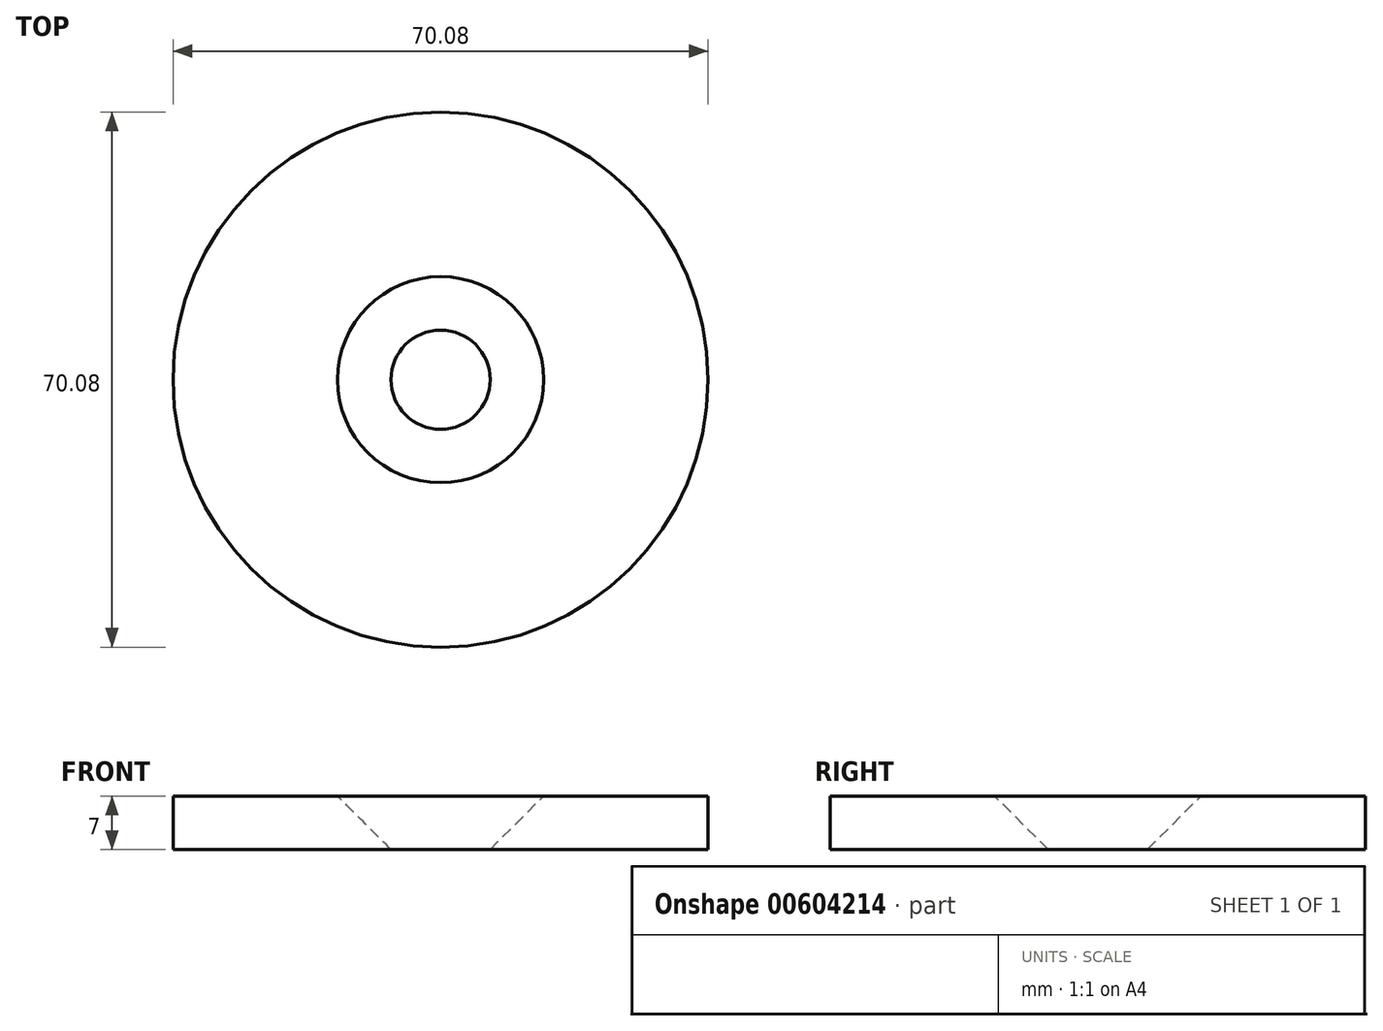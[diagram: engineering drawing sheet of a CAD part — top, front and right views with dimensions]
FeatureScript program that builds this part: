
annotation { "Feature Type Name" : "Feature", "Feature Type Description" : "" }
export const myFeature = defineFeature(function(context is Context, id is Id, definition is map)
    precondition{}
    {
        {
            var Q0;
            Q0=qCreatedBy(makeId("Front.planeOp"),FACE);
            var sketch = newSketch(context, id + "F0", { "sketchPlane" : qUnion([Q0])});
            skLineSegment(sketch, "E0", {"start": v(6.5, 0) * mm, "end": v(35.04, 0) * mm});
            skLineSegment(sketch, "E1", {"start": v(35.04, 0) * mm, "end": v(35.04, 7) * mm});
            skLineSegment(sketch, "E2", {"start": v(35.04, 7) * mm, "end": v(13.5, 7) * mm});
            skLineSegment(sketch, "E3", {"start": v(13.5, 7) * mm, "end": v(6.5, 0) * mm});
            skSolve(sketch);
        }
        {
            var Q0;
            Q0=qCreatedBy(makeId("Right.planeOp"),FACE);
            var sketch = newSketch(context, id + "F1", { "sketchPlane" : qUnion([Q0])});
            skLineSegment(sketch, "E4", {"start": v(0, 0) * mm, "end": v(0, 37.51) * mm, "construction": true});
            skSolve(sketch);
        }
        {
            var Q0;
            Q0=makeQuery(id+"F0.imprint","IMPRINT",FACE,{"disambiguationData":[TD([[makeQuery(id+"F0.imprint","IMPRINT",EDGE,{"derivedFrom":sQuery(id+"F0.wireOp",EDGE,"E0")}),1.0]])]});
            var Q1;
            Q1=sQuery(id+"F1.wireOp",EDGE,"E4");
            revolve(context, id + "F2", {"entities" : qUnion([Q0]), "axis" : qUnion([Q1]), "revolveType" : RevolveType.FULL});
        }
    });
